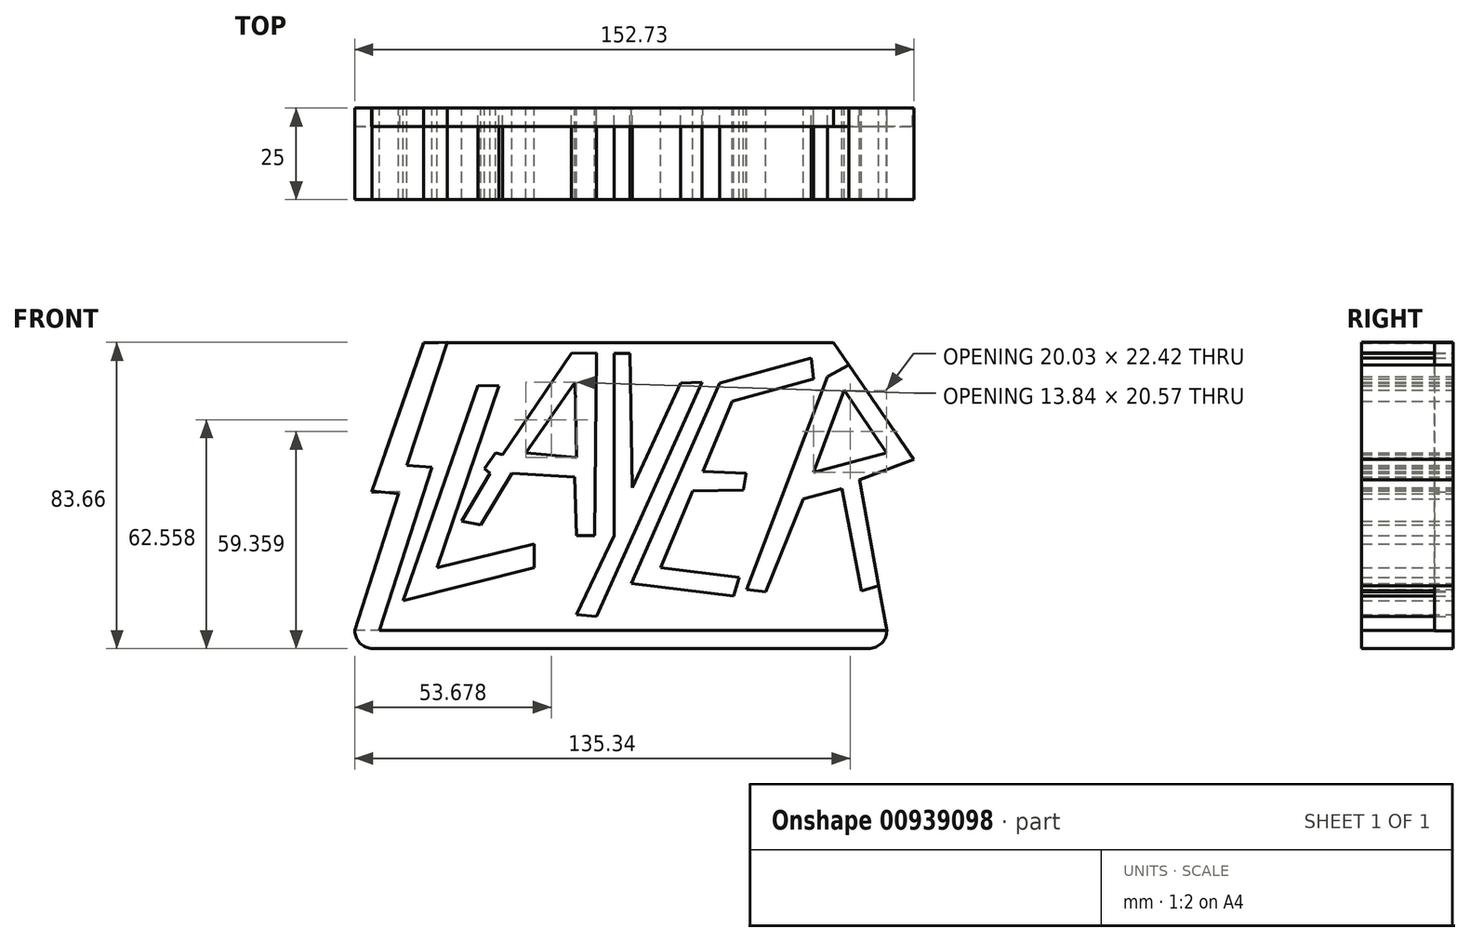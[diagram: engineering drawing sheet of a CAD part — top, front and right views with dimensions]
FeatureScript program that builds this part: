
annotation { "Feature Type Name" : "Feature", "Feature Type Description" : "" }
export const myFeature = defineFeature(function(context is Context, id is Id, definition is map)
    precondition{}
    {
        {
            var Q0;
            Q0=qCreatedBy(makeId("Front.planeOp"),FACE);
            var sketch = newSketch(context, id + "F0", { "sketchPlane" : qUnion([Q0])});
            skLineSegment(sketch, "E0", {"start": v(-56.41, 38.96) * mm, "end": v(-70.5, -1.52) * mm});
            skLineSegment(sketch, "E1", {"start": v(-70.5, -1.52) * mm, "end": v(-63.18, -2.18) * mm});
            skLineSegment(sketch, "E2", {"start": v(-63.18, -2.18) * mm, "end": v(-75.18, -39.55) * mm});
            skLineSegment(sketch, "E3", {"start": v(-75.18, -39.55) * mm, "end": v(-68.48, -39.55) * mm});
            skLineSegment(sketch, "E4", {"start": v(-68.48, -39.55) * mm, "end": v(-54.12, 4.97) * mm});
            skLineSegment(sketch, "E5", {"start": v(-54.12, 4.97) * mm, "end": v(-60.96, 5.49) * mm});
            skLineSegment(sketch, "E6", {"start": v(-60.96, 5.49) * mm, "end": v(-49.86, 39.1) * mm});
            skLineSegment(sketch, "E7", {"start": v(-49.86, 39.1) * mm, "end": v(-56.41, 38.96) * mm});
            skLineSegment(sketch, "E8", {"start": v(-35.83, 27.28) * mm, "end": v(-52.69, -22.42) * mm});
            skLineSegment(sketch, "E9", {"start": v(-52.69, -22.42) * mm, "end": v(-26.17, -16.01) * mm});
            skLineSegment(sketch, "E10", {"start": v(-26.17, -16.01) * mm, "end": v(-26.17, -22.42) * mm});
            skLineSegment(sketch, "E11", {"start": v(-26.17, -22.42) * mm, "end": v(-61.95, -31.51) * mm});
            skLineSegment(sketch, "E12", {"start": v(-61.95, -31.51) * mm, "end": v(-41.51, 27.34) * mm});
            skLineSegment(sketch, "E13", {"start": v(-41.51, 27.34) * mm, "end": v(-35.83, 27.28) * mm});
            skLineSegment(sketch, "E14", {"start": v(-16.04, 36.13) * mm, "end": v(-34.81, 8.42) * mm});
            skLineSegment(sketch, "E15", {"start": v(-34.81, 8.42) * mm, "end": v(-36.7, 8.94) * mm});
            skLineSegment(sketch, "E16", {"start": v(-36.7, 8.94) * mm, "end": v(-39.7, 4.67) * mm});
            skLineSegment(sketch, "E17", {"start": v(-39.7, 4.67) * mm, "end": v(-38.2, 3.38) * mm});
            skLineSegment(sketch, "E18", {"start": v(-38.2, 3.38) * mm, "end": v(-45.9, -9.76) * mm});
            skLineSegment(sketch, "E19", {"start": v(-45.9, -9.76) * mm, "end": v(-40.7, -10.77) * mm});
            skLineSegment(sketch, "E20", {"start": v(-40.7, -10.77) * mm, "end": v(-32.27, 3.38) * mm});
            skLineSegment(sketch, "E21", {"start": v(-32.27, 3.38) * mm, "end": v(-15.1, 2.36) * mm});
            skLineSegment(sketch, "E22", {"start": v(-15.1, 2.36) * mm, "end": v(-14.63, -13.66) * mm});
            skLineSegment(sketch, "E23", {"start": v(-14.63, -13.66) * mm, "end": v(-9.67, -13.66) * mm});
            skLineSegment(sketch, "E24", {"start": v(-9.67, -13.66) * mm, "end": v(-9.07, 36.24) * mm});
            skLineSegment(sketch, "E25", {"start": v(-9.07, 36.24) * mm, "end": v(-16.04, 36.13) * mm});
            skLineSegment(sketch, "E26", {"start": v(-4.34, 36.13) * mm, "end": v(-4.34, -13.66) * mm});
            skLineSegment(sketch, "E27", {"start": v(-4.34, -13.66) * mm, "end": v(-14.58, -35.32) * mm});
            skLineSegment(sketch, "E28", {"start": v(-14.58, -35.32) * mm, "end": v(-9.17, -35.74) * mm});
            skLineSegment(sketch, "E29", {"start": v(-9.17, -35.74) * mm, "end": v(19.68, 28.3) * mm});
            skLineSegment(sketch, "E30", {"start": v(19.68, 28.3) * mm, "end": v(13.87, 28.02) * mm});
            skLineSegment(sketch, "E31", {"start": v(13.87, 28.02) * mm, "end": v(0.68, -0.58) * mm});
            skLineSegment(sketch, "E32", {"start": v(0.68, -0.58) * mm, "end": v(0, 36.14) * mm});
            skLineSegment(sketch, "E33", {"start": v(0, 36.14) * mm, "end": v(-4.34, 36.13) * mm});
            skLineSegment(sketch, "E34", {"start": v(49.52, 34.82) * mm, "end": v(24.51, 28.02) * mm});
            skLineSegment(sketch, "E35", {"start": v(24.51, 28.02) * mm, "end": v(0.44, -26.75) * mm});
            skLineSegment(sketch, "E36", {"start": v(0.44, -26.75) * mm, "end": v(28.3, -30.15) * mm});
            skLineSegment(sketch, "E37", {"start": v(28.3, -30.15) * mm, "end": v(29.87, -25.1) * mm});
            skLineSegment(sketch, "E38", {"start": v(29.87, -25.1) * mm, "end": v(8.35, -22.42) * mm});
            skLineSegment(sketch, "E39", {"start": v(8.35, -22.42) * mm, "end": v(17.1, -1.52) * mm});
            skLineSegment(sketch, "E40", {"start": v(17.1, -1.52) * mm, "end": v(31, -1.26) * mm});
            skLineSegment(sketch, "E41", {"start": v(31, -1.26) * mm, "end": v(31.72, 3.38) * mm});
            skLineSegment(sketch, "E42", {"start": v(31.72, 3.38) * mm, "end": v(19.9, 3.85) * mm});
            skLineSegment(sketch, "E43", {"start": v(19.9, 3.85) * mm, "end": v(27.93, 23.08) * mm});
            skLineSegment(sketch, "E44", {"start": v(27.93, 23.08) * mm, "end": v(50.21, 29.14) * mm});
            skLineSegment(sketch, "E45", {"start": v(50.21, 29.14) * mm, "end": v(49.52, 34.82) * mm});
            skLineSegment(sketch, "E46", {"start": v(54, 29.8) * mm, "end": v(59.86, 32.96) * mm});
            skLineSegment(sketch, "E47", {"start": v(59.86, 32.96) * mm, "end": v(77.55, 7.13) * mm});
            skLineSegment(sketch, "E48", {"start": v(77.55, 7.13) * mm, "end": v(62.75, 1.52) * mm});
            skLineSegment(sketch, "E49", {"start": v(62.75, 1.52) * mm, "end": v(68, -27.42) * mm});
            skLineSegment(sketch, "E50", {"start": v(68, -27.42) * mm, "end": v(63.22, -28.73) * mm});
            skLineSegment(sketch, "E51", {"start": v(63.22, -28.73) * mm, "end": v(57.93, -0.83) * mm});
            skLineSegment(sketch, "E52", {"start": v(57.93, -0.83) * mm, "end": v(47.37, -3.7) * mm});
            skLineSegment(sketch, "E53", {"start": v(47.37, -3.7) * mm, "end": v(37.07, -29.07) * mm});
            skLineSegment(sketch, "E54", {"start": v(37.07, -29.07) * mm, "end": v(31.85, -28.43) * mm});
            skLineSegment(sketch, "E55", {"start": v(31.85, -28.43) * mm, "end": v(54, 29.8) * mm});
            skLineSegment(sketch, "E56", {"start": v(58.54, 26.02) * mm, "end": v(70.17, 8.94) * mm});
            skLineSegment(sketch, "E57", {"start": v(70.17, 8.94) * mm, "end": v(50.14, 3.6) * mm});
            skLineSegment(sketch, "E58", {"start": v(50.14, 3.6) * mm, "end": v(58.54, 26.02) * mm});
            skLineSegment(sketch, "E59", {"start": v(-14.58, 7.72) * mm, "end": v(-14.95, 28.3) * mm});
            skLineSegment(sketch, "E60", {"start": v(-14.95, 28.3) * mm, "end": v(-28.42, 8.94) * mm});
            skLineSegment(sketch, "E61", {"start": v(-28.42, 8.94) * mm, "end": v(-14.58, 7.72) * mm});
            skSolve(sketch);
        }
        {
            var Q0;
            Q0 = qSketchRegion(id + "F0", true);
            extrude(context, id + "F1", {"entities" : qUnion([Q0]), "depth" : 25 * mm, "offsetDistance" : 25 * mm});
        }
        {
            var Q0;
            Q0=makeQuery(id+"F1.opExtrude","SWEPT_FACE",FACE,{"disambiguationData":[OSD([sQuery(id+"F0.wireOp",EDGE,"E3")])]});
            var sketch = newSketch(context, id + "F2", { "sketchPlane" : qUnion([Q0])});
            skLineSegment(sketch, "E62.bottom", {"start": v(-75.18, 25) * mm, "end": v(70.2, 25) * mm});
            skLineSegment(sketch, "E62.top", {"start": v(-75.18, 0) * mm, "end": v(70.2, 0) * mm});
            skLineSegment(sketch, "E62.left", {"start": v(-75.18, 25) * mm, "end": v(-75.18, 0) * mm});
            skLineSegment(sketch, "E62.right", {"start": v(70.2, 25) * mm, "end": v(70.2, 0) * mm});
            skSolve(sketch);
        }
        {
            var Q0;
            Q0 = qSketchRegion(id + "F2", true);
            extrude(context, id + "F3", {"entities" : qUnion([Q0]), "operationType" : NewBodyOperationType.ADD, "depth" : 5 * mm, "offsetDistance" : 25 * mm});
        }
        {
            var Q0;
            Q0=qCreatedBy(makeId("Front.planeOp"),FACE);
            var sketch = newSketch(context, id + "F4", { "sketchPlane" : qUnion([Q0])});
            skLineSegment(sketch, "E63", {"start": v(-75.13, -39.55) * mm, "end": v(-62.83, -1.71) * mm});
            skLineSegment(sketch, "E64", {"start": v(-62.83, -1.71) * mm, "end": v(-70.55, -1.71) * mm});
            skLineSegment(sketch, "E65", {"start": v(-70.55, -1.71) * mm, "end": v(-56.44, 39.05) * mm});
            skLineSegment(sketch, "E66", {"start": v(-56.44, 39.05) * mm, "end": v(55.6, 39.05) * mm});
            skLineSegment(sketch, "E67", {"start": v(55.6, 39.05) * mm, "end": v(77.17, 7.2) * mm});
            skLineSegment(sketch, "E68", {"start": v(77.17, 7.2) * mm, "end": v(62.51, 1.7) * mm});
            skLineSegment(sketch, "E69", {"start": v(62.51, 1.7) * mm, "end": v(70.27, -39.67) * mm});
            skLineSegment(sketch, "E70", {"start": v(70.27, -39.67) * mm, "end": v(-75.13, -39.55) * mm});
            skSolve(sketch);
        }
        {
            var Q0;
            Q0 = qSketchRegion(id + "F4", true);
            extrude(context, id + "F5", {"entities" : qUnion([Q0]), "depth" : 5 * mm, "offsetDistance" : 25 * mm});
        }
        {
            var Q0;
            Q0=makeQuery(id+"F3.opExtrude","CAP_EDGE",EDGE,{"disambiguationData":[OSD([sQuery(id+"F2.wireOp",EDGE,"E62.right")])],"isStart":false});
            var Q1;
            Q1=makeQuery(id+"F3.opExtrude","CAP_EDGE",EDGE,{"disambiguationData":[OSD([sQuery(id+"F2.wireOp",EDGE,"E62.left")])],"isStart":false});
            fillet(context, id + "F6", {"entities" : qUnion([Q0, Q1]), "radius" : 5 * mm, "tangentPropagation" : true, "allowEdgeOverflow" : false});
        }
    });
